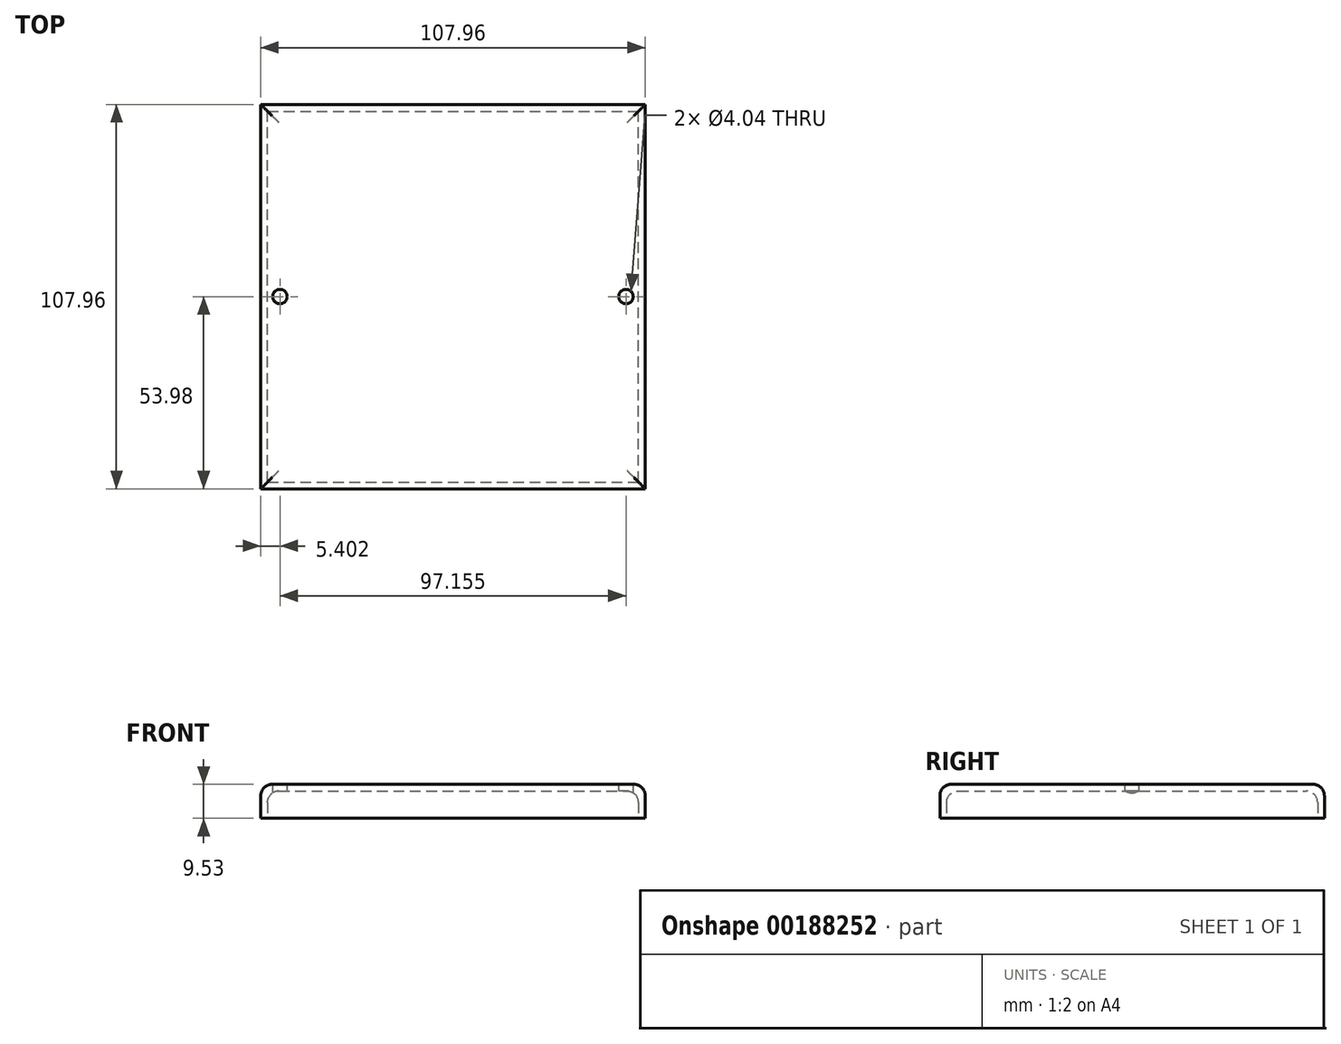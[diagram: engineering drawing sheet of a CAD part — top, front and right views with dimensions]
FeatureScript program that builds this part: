
annotation { "Feature Type Name" : "Feature", "Feature Type Description" : "" }
export const myFeature = defineFeature(function(context is Context, id is Id, definition is map)
    precondition{}
    {
        {
            var Q0;
            Q0=qCreatedBy(makeId("Top.planeOp"),FACE);
            var sketch = newSketch(context, id + "F0", { "sketchPlane" : qUnion([Q0])});
            skLineSegment(sketch, "E0.bottom", {"start": v(-53.97, 53.98) * mm, "end": v(53.98, 53.98) * mm});
            skLineSegment(sketch, "E0.top", {"start": v(-53.98, -53.98) * mm, "end": v(53.97, -53.98) * mm});
            skLineSegment(sketch, "E0.left", {"start": v(-53.97, 53.98) * mm, "end": v(-53.98, -53.98) * mm});
            skLineSegment(sketch, "E0.right", {"start": v(53.98, 53.98) * mm, "end": v(53.97, -53.98) * mm});
            skPoint(sketch, "E0.middle", {"position": v(0, 0) * mm});
            skSolve(sketch);
        }
        {
            var Q0;
            Q0 = qSketchRegion(id + "F0", true);
            extrude(context, id + "F1", {"entities" : qUnion([Q0]), "depth" : 9.52 * mm});
        }
        {
            var Q0;
            Q0=makeQuery(id+"F1.opExtrude","CAP_FACE",FACE,{"disambiguationData":[OSD([sQuery(id+"F0.wireOp",EDGE,"E0.bottom"),sQuery(id+"F0.wireOp",EDGE,"E0.top"),sQuery(id+"F0.wireOp",EDGE,"E0.left"),sQuery(id+"F0.wireOp",EDGE,"E0.right")])],"isStart":true});
            var sketch = newSketch(context, id + "F2", { "sketchPlane" : qUnion([Q0])});
            skLineSegment(sketch, "E1.bottom", {"start": v(-52.08, 52.08) * mm, "end": v(52.08, 52.08) * mm});
            skLineSegment(sketch, "E1.top", {"start": v(-52.08, -52.08) * mm, "end": v(52.08, -52.08) * mm});
            skLineSegment(sketch, "E1.left", {"start": v(-52.08, 52.08) * mm, "end": v(-52.08, -52.08) * mm});
            skLineSegment(sketch, "E1.right", {"start": v(52.08, 52.08) * mm, "end": v(52.08, -52.08) * mm});
            skPoint(sketch, "E1.middle", {"position": v(0, 0) * mm});
            skSolve(sketch);
        }
        {
            var Q0;
            Q0 = qSketchRegion(id + "F2", true);
            extrude(context, id + "F3", {"entities" : qUnion([Q0]), "operationType" : NewBodyOperationType.REMOVE, "oppositeDirection" : true, "depth" : 7.63 * mm});
        }
        {
            var Q0;
            Q0=makeQuery(id+"F3.boolean.opBoolean","COPY",FACE,{"derivedFrom":makeQuery(id+"F3.opExtrude","CAP_FACE",FACE,{"disambiguationData":[OSD([sQuery(id+"F2.wireOp",EDGE,"E1.bottom"),sQuery(id+"F2.wireOp",EDGE,"E1.top"),sQuery(id+"F2.wireOp",EDGE,"E1.left"),sQuery(id+"F2.wireOp",EDGE,"E1.right")])],"isStart":false})});
            var Q1;
            Q1=makeQuery(id+"F1.opExtrude","CAP_FACE",FACE,{"disambiguationData":[OSD([sQuery(id+"F0.wireOp",EDGE,"E0.bottom"),sQuery(id+"F0.wireOp",EDGE,"E0.top"),sQuery(id+"F0.wireOp",EDGE,"E0.left"),sQuery(id+"F0.wireOp",EDGE,"E0.right")])],"isStart":false});
            fillet(context, id + "F4", {"entities" : qUnion([Q0, Q1]), "radius" : 3.17 * mm, "tangentPropagation" : true, "allowEdgeOverflow" : false});
        }
        {
            var Q0;
            Q0=makeQuery(id+"F1.opExtrude","CAP_FACE",FACE,{"disambiguationData":[OSD([sQuery(id+"F0.wireOp",EDGE,"E0.bottom"),sQuery(id+"F0.wireOp",EDGE,"E0.top"),sQuery(id+"F0.wireOp",EDGE,"E0.left"),sQuery(id+"F0.wireOp",EDGE,"E0.right")])],"isStart":false});
            var sketch = newSketch(context, id + "F5", { "sketchPlane" : qUnion([Q0])});
            skPoint(sketch, "E2", {"position": v(-48.58, 0) * mm});
            skPoint(sketch, "E3", {"position": v(48.58, 0) * mm});
            skSolve(sketch);
        }
        {
            var Q0;
            Q0=sQuery(id+"F5.wireOp",VERTEX,"E2");
            var Q1;
            Q1=sQuery(id+"F5.wireOp",VERTEX,"E3");
            var Q2;
            Q2=makeQuery(id+"F1.opExtrude","SWEPT_BODY",BODY,{"disambiguationData":[OSD([sQuery(id+"F0.wireOp",EDGE,"E0.bottom"),sQuery(id+"F0.wireOp",EDGE,"E0.top"),sQuery(id+"F0.wireOp",EDGE,"E0.left"),sQuery(id+"F0.wireOp",EDGE,"E0.right")])]});
            hole(context, id + "F6", {"style" : HoleStyle.SIMPLE, "endStyle" : HoleEndStyle.BLIND, "standardTappedOrClearance" : lookupTablePath({ "standard" : "ANSI", "engagement" : "75%", "pitch" : "32 tpi", "size" : "#10", "type" : "Tapped" }), "standardBlindInLast" : lookupTablePath({ "standard" : "ANSI", "engagement" : "75%", "pitch" : "32 tpi", "size" : "#10", "type" : "Tapped" }), "holeDiameter" : 4.04 * mm, "holeDepth" : 8.9 * mm, "locations" : qUnion([Q0, Q1]), "scope" : qUnion([Q2]), "majorDiameter" : 4.83 * mm});
        }
    });
